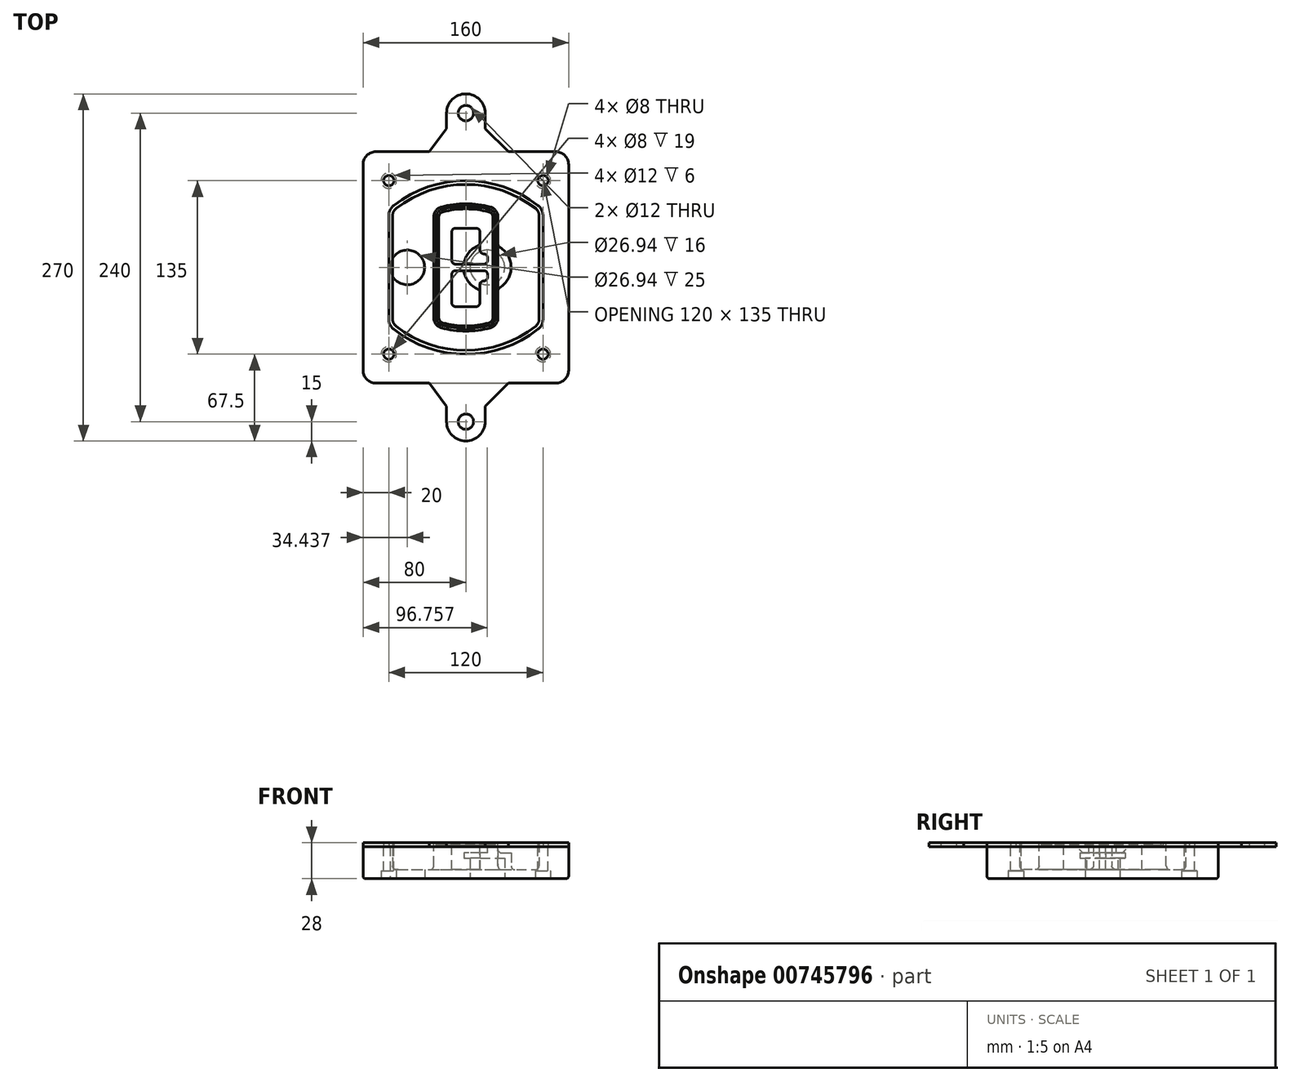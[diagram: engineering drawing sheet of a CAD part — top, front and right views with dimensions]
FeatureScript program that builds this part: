
annotation { "Feature Type Name" : "Feature", "Feature Type Description" : "" }
export const myFeature = defineFeature(function(context is Context, id is Id, definition is map)
    precondition{}
    {
        {
            var Q0;
            Q0=qCreatedBy(makeId("Top.planeOp"),FACE);
            var sketch = newSketch(context, id + "F0", { "sketchPlane" : qUnion([Q0])});
            skPoint(sketch, "E0.rect.middle", {"position": v(0, 0) * mm});
            skLineSegment(sketch, "E1.bottom", {"start": v(-70, -90) * mm, "end": v(70, -90) * mm});
            skLineSegment(sketch, "E1.top", {"start": v(-70, 90) * mm, "end": v(70, 90) * mm});
            skLineSegment(sketch, "E1.left", {"start": v(-80, -80) * mm, "end": v(-80, 80) * mm});
            skLineSegment(sketch, "E1.right", {"start": v(80, -80) * mm, "end": v(80, 80) * mm});
            skLineSegment(sketch, "E2", {"start": v(-80, 90) * mm, "end": v(80, -90) * mm, "construction": true});
            skLineSegment(sketch, "E3", {"start": v(80, 90) * mm, "end": v(-80, -90) * mm, "construction": true});
            skCircle(sketch, "E4", {"center": v(-60, 67.5) * mm, "radius": 4 * mm});
            skCircle(sketch, "E5", {"center": v(60, 67.5) * mm, "radius": 4 * mm});
            skCircle(sketch, "E6", {"center": v(60, -67.5) * mm, "radius": 4 * mm});
            skCircle(sketch, "E7", {"center": v(-60, -67.5) * mm, "radius": 4 * mm});
            skLineSegment(sketch, "E8", {"start": v(-60, 67.5) * mm, "end": v(60, 67.5) * mm, "construction": true});
            skLineSegment(sketch, "E9", {"start": v(60, 67.5) * mm, "end": v(60, -67.5) * mm, "construction": true});
            skLineSegment(sketch, "E10", {"start": v(60, -67.5) * mm, "end": v(-60, -67.5) * mm, "construction": true});
            skLineSegment(sketch, "E11", {"start": v(-60, -67.5) * mm, "end": v(-60, 67.5) * mm, "construction": true});
            skLineSegment(sketch, "E12", {"start": v(-60, 40.3) * mm, "end": v(-60, -40.3) * mm});
            skLineSegment(sketch, "E13", {"start": v(60, 40.3) * mm, "end": v(60, -40.3) * mm});
            skArc(sketch, "E14", {"start": v(56.15, 48.18) * mm, "mid": v(0, 67.5) * mm, "end": v(-56.15, 48.18) * mm});
            skArc(sketch, "E15", {"start": v(-56.15, -48.18) * mm, "mid": v(0, -67.5) * mm, "end": v(56.15, -48.18) * mm});
            skLineSegment(sketch, "E16", {"start": v(-60, 0) * mm, "end": v(60, 0) * mm, "construction": true});
            skPoint(sketch, "E17.visualSharp", {"position": v(-60, -45) * mm});
            skArc(sketch, "E17.filletArc", {"start": v(-60, -40.3) * mm, "mid": v(-58.99, -44.68) * mm, "end": v(-56.15, -48.18) * mm});
            skPoint(sketch, "E18.visualSharp", {"position": v(-60, 45) * mm});
            skArc(sketch, "E18.filletArc", {"start": v(-56.15, 48.18) * mm, "mid": v(-58.99, 44.68) * mm, "end": v(-60, 40.3) * mm});
            skPoint(sketch, "E19.visualSharp", {"position": v(60, 45) * mm});
            skArc(sketch, "E19.filletArc", {"start": v(60, 40.3) * mm, "mid": v(58.99, 44.68) * mm, "end": v(56.15, 48.18) * mm});
            skPoint(sketch, "E20.visualSharp", {"position": v(60, -45) * mm});
            skArc(sketch, "E20.filletArc", {"start": v(56.15, -48.18) * mm, "mid": v(58.99, -44.68) * mm, "end": v(60, -40.3) * mm});
            skPoint(sketch, "E21.visualSharp", {"position": v(-80, 90) * mm});
            skArc(sketch, "E21.filletArc", {"start": v(-70, 90) * mm, "mid": v(-77.07, 87.07) * mm, "end": v(-80, 80) * mm});
            skPoint(sketch, "E22.visualSharp", {"position": v(80, 90) * mm});
            skArc(sketch, "E22.filletArc", {"start": v(80, 80) * mm, "mid": v(77.07, 87.07) * mm, "end": v(70, 90) * mm});
            skPoint(sketch, "E23.visualSharp", {"position": v(80, -90) * mm});
            skArc(sketch, "E23.filletArc", {"start": v(70, -90) * mm, "mid": v(77.07, -87.07) * mm, "end": v(80, -80) * mm});
            skPoint(sketch, "E24.visualSharp", {"position": v(-80, -90) * mm});
            skArc(sketch, "E24.filletArc", {"start": v(-80, -80) * mm, "mid": v(-77.07, -87.07) * mm, "end": v(-70, -90) * mm});
            skArc(sketch, "E25.0", {"start": v(57, 40.3) * mm, "mid": v(56.3, 43.36) * mm, "end": v(54.3, 45.81) * mm});
            skLineSegment(sketch, "E25.1", {"start": v(57, 40.3) * mm, "end": v(57, -40.3) * mm});
            skArc(sketch, "E25.2", {"start": v(54.3, -45.81) * mm, "mid": v(56.3, -43.36) * mm, "end": v(57, -40.3) * mm});
            skArc(sketch, "E25.3", {"start": v(-54.3, -45.81) * mm, "mid": v(0, -64.5) * mm, "end": v(54.3, -45.81) * mm});
            skArc(sketch, "E25.4", {"start": v(-57, -40.3) * mm, "mid": v(-56.3, -43.36) * mm, "end": v(-54.3, -45.81) * mm});
            skArc(sketch, "E25.5", {"start": v(54.3, 45.81) * mm, "mid": v(0, 64.5) * mm, "end": v(-54.3, 45.81) * mm});
            skLineSegment(sketch, "E25.6", {"start": v(-57, 40.3) * mm, "end": v(-57, -40.3) * mm});
            skArc(sketch, "E25.7", {"start": v(-54.3, 45.81) * mm, "mid": v(-56.3, 43.36) * mm, "end": v(-57, 40.3) * mm});
            skArc(sketch, "E26.0", {"start": v(-58.62, 51.33) * mm, "mid": v(-62.58, 46.43) * mm, "end": v(-64, 40.3) * mm});
            skArc(sketch, "E26.1", {"start": v(58.62, 51.33) * mm, "mid": v(0, 71.5) * mm, "end": v(-58.62, 51.33) * mm});
            skArc(sketch, "E26.2", {"start": v(64, 40.3) * mm, "mid": v(62.58, 46.43) * mm, "end": v(58.62, 51.33) * mm});
            skLineSegment(sketch, "E26.3", {"start": v(64, 40.3) * mm, "end": v(64, -40.3) * mm});
            skArc(sketch, "E26.4", {"start": v(58.62, -51.33) * mm, "mid": v(62.58, -46.43) * mm, "end": v(64, -40.3) * mm});
            skLineSegment(sketch, "E26.5", {"start": v(-64, 40.3) * mm, "end": v(-64, -40.3) * mm});
            skArc(sketch, "E26.6", {"start": v(-58.62, -51.33) * mm, "mid": v(0, -71.5) * mm, "end": v(58.62, -51.33) * mm});
            skArc(sketch, "E26.7", {"start": v(-64, -40.3) * mm, "mid": v(-62.58, -46.43) * mm, "end": v(-58.62, -51.33) * mm});
            skSolve(sketch);
        }
        {
            var Q0;
            Q0=makeQuery(id+"F0.imprint","IMPRINT",FACE,{"disambiguationData":[TD([[makeQuery(id+"F0.imprint","IMPRINT",EDGE,{"derivedFrom":sQuery(id+"F0.wireOp",EDGE,"E1.bottom")}),1.0]])]});
            var Q1;
            Q1=makeQuery(id+"F0.imprint","IMPRINT",FACE,{"disambiguationData":[TD([[makeQuery(id+"F0.imprint","IMPRINT",EDGE,{"derivedFrom":sQuery(id+"F0.wireOp",EDGE,"E12")}),1.0]])]});
            var Q2;
            Q2=makeQuery(id+"F0.imprint","IMPRINT",FACE,{"disambiguationData":[TD([[makeQuery(id+"F0.imprint","IMPRINT",EDGE,{"derivedFrom":sQuery(id+"F0.wireOp",EDGE,"E25.0")}),1.0]])]});
            var Q3;
            Q3=makeQuery(id+"F0.imprint","IMPRINT",FACE,{"disambiguationData":[TD([[makeQuery(id+"F0.imprint","IMPRINT",EDGE,{"derivedFrom":sQuery(id+"F0.wireOp",EDGE,"E12")}),-1.0]])]});
            extrude(context, id + "F1", {"entities" : qUnion([Q0, Q1, Q2, Q3]), "oppositeDirection" : true, "depth" : 25 * mm});
        }
        {
            var Q0;
            Q0=makeQuery(id+"F0.imprint","IMPRINT",FACE,{"disambiguationData":[TD([[makeQuery(id+"F0.imprint","IMPRINT",EDGE,{"derivedFrom":sQuery(id+"F0.wireOp",EDGE,"E12")}),1.0]])]});
            extrude(context, id + "F2", {"entities" : qUnion([Q0]), "operationType" : NewBodyOperationType.ADD, "depth" : 3 * mm, "offsetDistance" : 25 * mm});
        }
        {
            var Q0;
            Q0=makeQuery(id+"F0.imprint","IMPRINT",FACE,{"disambiguationData":[TD([[makeQuery(id+"F0.imprint","IMPRINT",EDGE,{"derivedFrom":sQuery(id+"F0.wireOp",EDGE,"E25.0")}),1.0]])]});
            extrude(context, id + "F3", {"entities" : qUnion([Q0]), "operationType" : NewBodyOperationType.REMOVE, "oppositeDirection" : true, "depth" : 18 * mm});
        }
        {
            var Q0;
            Q0=makeQuery(id+"F2.opExtrude","CAP_FACE",FACE,{"disambiguationData":[OSD([sQuery(id+"F0.wireOp",EDGE,"E12"),sQuery(id+"F0.wireOp",EDGE,"E13"),sQuery(id+"F0.wireOp",EDGE,"E14"),sQuery(id+"F0.wireOp",EDGE,"E15"),sQuery(id+"F0.wireOp",EDGE,"E17.filletArc"),sQuery(id+"F0.wireOp",EDGE,"E18.filletArc"),sQuery(id+"F0.wireOp",EDGE,"E19.filletArc"),sQuery(id+"F0.wireOp",EDGE,"E20.filletArc"),sQuery(id+"F0.wireOp",EDGE,"E25.0"),sQuery(id+"F0.wireOp",EDGE,"E25.1"),sQuery(id+"F0.wireOp",EDGE,"E25.2"),sQuery(id+"F0.wireOp",EDGE,"E25.3"),sQuery(id+"F0.wireOp",EDGE,"E25.4"),sQuery(id+"F0.wireOp",EDGE,"E25.5"),sQuery(id+"F0.wireOp",EDGE,"E25.6"),sQuery(id+"F0.wireOp",EDGE,"E25.7")])],"isStart":false});
            var sketch = newSketch(context, id + "F4", { "sketchPlane" : qUnion([Q0])});
            skArc(sketch, "E27.0", {"start": v(-19.08, -46.97) * mm, "mid": v(0, -49.5) * mm, "end": v(19.08, -46.97) * mm});
            skArc(sketch, "E28.0", {"start": v(19.08, 46.97) * mm, "mid": v(0, 49.5) * mm, "end": v(-19.08, 46.97) * mm});
            skLineSegment(sketch, "E29", {"start": v(-25, 39.25) * mm, "end": v(-25, -39.25) * mm});
            skLineSegment(sketch, "E30", {"start": v(25, 39.25) * mm, "end": v(25, -39.25) * mm});
            skLineSegment(sketch, "E31", {"start": v(-25, 45.1) * mm, "end": v(25, 45.1) * mm, "construction": true});
            skLineSegment(sketch, "E32", {"start": v(-25, -45.1) * mm, "end": v(25, -45.1) * mm, "construction": true});
            skPoint(sketch, "E33.visualSharp", {"position": v(-25, 45.1) * mm});
            skArc(sketch, "E33.filletArc", {"start": v(-19.08, 46.97) * mm, "mid": v(-23.35, 44.11) * mm, "end": v(-25, 39.25) * mm});
            skPoint(sketch, "E34.visualSharp", {"position": v(25, 45.1) * mm});
            skArc(sketch, "E34.filletArc", {"start": v(25, 39.25) * mm, "mid": v(23.35, 44.11) * mm, "end": v(19.08, 46.97) * mm});
            skPoint(sketch, "E35.visualSharp", {"position": v(25, -45.1) * mm});
            skArc(sketch, "E35.filletArc", {"start": v(19.08, -46.97) * mm, "mid": v(23.35, -44.11) * mm, "end": v(25, -39.25) * mm});
            skPoint(sketch, "E36.visualSharp", {"position": v(-25, -45.1) * mm});
            skArc(sketch, "E36.filletArc", {"start": v(-25, -39.25) * mm, "mid": v(-23.35, -44.11) * mm, "end": v(-19.08, -46.97) * mm});
            skArc(sketch, "E37.0", {"start": v(54.3, 45.81) * mm, "mid": v(0, 64.5) * mm, "end": v(-54.3, 45.81) * mm});
            skArc(sketch, "E37.1", {"start": v(-54.3, 45.81) * mm, "mid": v(-56.3, 43.36) * mm, "end": v(-57, 40.3) * mm});
            skLineSegment(sketch, "E37.2", {"start": v(-57, 40.3) * mm, "end": v(-57, -40.3) * mm});
            skArc(sketch, "E37.3", {"start": v(-57, -40.3) * mm, "mid": v(-56.3, -43.36) * mm, "end": v(-54.3, -45.81) * mm});
            skArc(sketch, "E37.4", {"start": v(-54.3, -45.81) * mm, "mid": v(0, -64.5) * mm, "end": v(54.3, -45.81) * mm});
            skArc(sketch, "E37.5", {"start": v(54.3, -45.81) * mm, "mid": v(56.3, -43.36) * mm, "end": v(57, -40.3) * mm});
            skLineSegment(sketch, "E37.6", {"start": v(57, 40.3) * mm, "end": v(57, -40.3) * mm});
            skArc(sketch, "E37.7", {"start": v(57, 40.3) * mm, "mid": v(56.3, 43.36) * mm, "end": v(54.3, 45.81) * mm});
            skLineSegment(sketch, "E38.0", {"start": v(23, 39.25) * mm, "end": v(23, -39.25) * mm});
            skArc(sketch, "E38.1", {"start": v(18.56, -45.04) * mm, "mid": v(21.76, -42.9) * mm, "end": v(23, -39.25) * mm});
            skArc(sketch, "E38.2", {"start": v(-18.56, -45.04) * mm, "mid": v(0, -47.5) * mm, "end": v(18.56, -45.04) * mm});
            skArc(sketch, "E38.3", {"start": v(-23, -39.25) * mm, "mid": v(-21.76, -42.9) * mm, "end": v(-18.56, -45.04) * mm});
            skLineSegment(sketch, "E38.4", {"start": v(-23, 39.25) * mm, "end": v(-23, -39.25) * mm});
            skArc(sketch, "E38.5", {"start": v(23, 39.25) * mm, "mid": v(21.76, 42.9) * mm, "end": v(18.56, 45.04) * mm});
            skArc(sketch, "E38.6", {"start": v(-18.56, 45.04) * mm, "mid": v(-21.76, 42.9) * mm, "end": v(-23, 39.25) * mm});
            skArc(sketch, "E38.7", {"start": v(18.56, 45.04) * mm, "mid": v(0, 47.5) * mm, "end": v(-18.56, 45.04) * mm});
            skArc(sketch, "E39.0", {"start": v(21, 39.25) * mm, "mid": v(20.18, 41.68) * mm, "end": v(18.04, 43.1) * mm});
            skLineSegment(sketch, "E39.1", {"start": v(21, 39.25) * mm, "end": v(21, -39.25) * mm});
            skArc(sketch, "E39.2", {"start": v(18.04, -43.1) * mm, "mid": v(20.18, -41.68) * mm, "end": v(21, -39.25) * mm});
            skArc(sketch, "E39.3", {"start": v(-18.04, -43.1) * mm, "mid": v(0, -45.5) * mm, "end": v(18.04, -43.1) * mm});
            skArc(sketch, "E39.4", {"start": v(-21, -39.25) * mm, "mid": v(-20.18, -41.68) * mm, "end": v(-18.04, -43.1) * mm});
            skArc(sketch, "E39.5", {"start": v(18.04, 43.1) * mm, "mid": v(0, 45.5) * mm, "end": v(-18.04, 43.1) * mm});
            skLineSegment(sketch, "E39.6", {"start": v(-21, 39.25) * mm, "end": v(-21, -39.25) * mm});
            skArc(sketch, "E39.7", {"start": v(-18.04, 43.1) * mm, "mid": v(-20.18, 41.68) * mm, "end": v(-21, 39.25) * mm});
            skLineSegment(sketch, "E40", {"start": v(-25, 0) * mm, "end": v(25, 0) * mm, "construction": true});
            skLineSegment(sketch, "E41", {"start": v(-11, 5.5) * mm, "end": v(-11, 27.5) * mm});
            skLineSegment(sketch, "E42", {"start": v(-8, 30.5) * mm, "end": v(8, 30.5) * mm});
            skLineSegment(sketch, "E43", {"start": v(11, 27.5) * mm, "end": v(11, 13.5) * mm});
            skLineSegment(sketch, "E44", {"start": v(14, 10.5) * mm, "end": v(14, 10.5) * mm});
            skLineSegment(sketch, "E45", {"start": v(17, 7.5) * mm, "end": v(17, 5.5) * mm});
            skLineSegment(sketch, "E46", {"start": v(14, 2.5) * mm, "end": v(-8, 2.5) * mm});
            skPoint(sketch, "E47.visualSharp", {"position": v(-11, 30.5) * mm});
            skArc(sketch, "E47.filletArc", {"start": v(-8, 30.5) * mm, "mid": v(-10.12, 29.62) * mm, "end": v(-11, 27.5) * mm});
            skPoint(sketch, "E48.visualSharp", {"position": v(11, 30.5) * mm});
            skArc(sketch, "E48.filletArc", {"start": v(11, 27.5) * mm, "mid": v(10.12, 29.62) * mm, "end": v(8, 30.5) * mm});
            skPoint(sketch, "E49.visualSharp", {"position": v(11, 10.5) * mm});
            skArc(sketch, "E49.filletArc", {"start": v(11, 13.5) * mm, "mid": v(11.88, 11.38) * mm, "end": v(14, 10.5) * mm});
            skPoint(sketch, "E50.visualSharp", {"position": v(17, 10.5) * mm});
            skArc(sketch, "E50.filletArc", {"start": v(17, 7.5) * mm, "mid": v(16.12, 9.62) * mm, "end": v(14, 10.5) * mm});
            skPoint(sketch, "E51.visualSharp", {"position": v(17, 2.5) * mm});
            skArc(sketch, "E51.filletArc", {"start": v(14, 2.5) * mm, "mid": v(16.12, 3.38) * mm, "end": v(17, 5.5) * mm});
            skPoint(sketch, "E52.visualSharp", {"position": v(-11, 2.5) * mm});
            skArc(sketch, "E52.filletArc", {"start": v(-11, 5.5) * mm, "mid": v(-10.12, 3.38) * mm, "end": v(-8, 2.5) * mm});
            skLineSegment(sketch, "E53.0.MirrorCS", {"start": v(14, -2.5) * mm, "end": v(-8, -2.5) * mm});
            skArc(sketch, "E54.0.MirrorCS", {"start": v(-11, -5.5) * mm, "mid": v(-10.12, -3.38) * mm, "end": v(-8, -2.5) * mm});
            skLineSegment(sketch, "E55.0.MirrorCS", {"start": v(-11, -5.5) * mm, "end": v(-11, -27.5) * mm});
            skArc(sketch, "E56.0.MirrorCS", {"start": v(-8, -30.5) * mm, "mid": v(-10.12, -29.62) * mm, "end": v(-11, -27.5) * mm});
            skLineSegment(sketch, "E57.0.MirrorCS", {"start": v(-8, -30.5) * mm, "end": v(8, -30.5) * mm});
            skArc(sketch, "E58.0.MirrorCS", {"start": v(11, -27.5) * mm, "mid": v(10.12, -29.62) * mm, "end": v(8, -30.5) * mm});
            skLineSegment(sketch, "E59.0.MirrorCS", {"start": v(11, -27.5) * mm, "end": v(11, -13.5) * mm});
            skArc(sketch, "E60.0.MirrorCS", {"start": v(11, -13.5) * mm, "mid": v(11.88, -11.38) * mm, "end": v(14, -10.5) * mm});
            skArc(sketch, "E61.0.MirrorCS", {"start": v(17, -7.5) * mm, "mid": v(16.12, -9.62) * mm, "end": v(14, -10.5) * mm});
            skLineSegment(sketch, "E62.0.MirrorCS", {"start": v(17, -7.5) * mm, "end": v(17, -5.5) * mm});
            skArc(sketch, "E63.0.MirrorCS", {"start": v(14, -2.5) * mm, "mid": v(16.12, -3.38) * mm, "end": v(17, -5.5) * mm});
            skSolve(sketch);
        }
        {
            var Q0;
            Q0=makeQuery(id+"F4.imprint","IMPRINT",FACE,{"disambiguationData":[TD([[makeQuery(id+"F4.imprint","IMPRINT",EDGE,{"derivedFrom":sQuery(id+"F4.wireOp",EDGE,"E27.0")}),1.0]])]});
            var Q1;
            Q1=makeQuery(id+"F4.imprint","IMPRINT",FACE,{"disambiguationData":[TD([[makeQuery(id+"F4.imprint","IMPRINT",EDGE,{"derivedFrom":sQuery(id+"F4.wireOp",EDGE,"E38.0")}),-1.0]])]});
            var Q2;
            Q2=makeQuery(id+"F4.imprint","IMPRINT",FACE,{"disambiguationData":[TD([[makeQuery(id+"F4.imprint","IMPRINT",EDGE,{"derivedFrom":sQuery(id+"F4.wireOp",EDGE,"E39.0")}),1.0]])]});
            extrude(context, id + "F5", {"entities" : qUnion([Q0, Q1, Q2]), "operationType" : NewBodyOperationType.ADD, "endBound" : BoundingType.UP_TO_NEXT, "oppositeDirection" : true, "depth" : 25 * mm});
        }
        {
            var Q0;
            Q0=makeQuery(id+"F4.imprint","IMPRINT",FACE,{"disambiguationData":[TD([[makeQuery(id+"F4.imprint","IMPRINT",EDGE,{"derivedFrom":sQuery(id+"F4.wireOp",EDGE,"E38.0")}),-1.0]])]});
            extrude(context, id + "F6", {"entities" : qUnion([Q0]), "operationType" : NewBodyOperationType.REMOVE, "oppositeDirection" : true, "depth" : 2 * mm});
        }
        {
            var Q0;
            Q0=makeQuery(id+"F1.opExtrude","CAP_FACE",FACE,{"disambiguationData":[OSD([sQuery(id+"F0.wireOp",EDGE,"E1.bottom"),sQuery(id+"F0.wireOp",EDGE,"E1.top"),sQuery(id+"F0.wireOp",EDGE,"E1.left"),sQuery(id+"F0.wireOp",EDGE,"E1.right"),sQuery(id+"F0.wireOp",EDGE,"E4"),sQuery(id+"F0.wireOp",EDGE,"E5"),sQuery(id+"F0.wireOp",EDGE,"E6"),sQuery(id+"F0.wireOp",EDGE,"E7"),sQuery(id+"F0.wireOp",EDGE,"E21.filletArc"),sQuery(id+"F0.wireOp",EDGE,"E22.filletArc"),sQuery(id+"F0.wireOp",EDGE,"E23.filletArc"),sQuery(id+"F0.wireOp",EDGE,"E24.filletArc")])],"isStart":false});
            var sketch = newSketch(context, id + "F7", { "sketchPlane" : qUnion([Q0])});
            skCircle(sketch, "E64", {"center": v(16.76, 0) * mm, "radius": 13.47 * mm});
            skCircle(sketch, "E65", {"center": v(-45.56, 0) * mm, "radius": 13.47 * mm});
            skLineSegment(sketch, "E66", {"start": v(80, 0) * mm, "end": v(-80, 0) * mm});
            skCircle(sketch, "E67", {"center": v(16.76, 0) * mm, "radius": 18.47 * mm});
            skCircle(sketch, "E68", {"center": v(60, -67.5) * mm, "radius": 6 * mm});
            skCircle(sketch, "E69", {"center": v(-60, -67.5) * mm, "radius": 6 * mm});
            skCircle(sketch, "E70", {"center": v(-60, 67.5) * mm, "radius": 6 * mm});
            skCircle(sketch, "E71", {"center": v(60, 67.5) * mm, "radius": 6 * mm});
            skSolve(sketch);
        }
        {
            var Q0;
            {var subQ1=sQuery(id+"F7.wireOp",EDGE,"E66");var subQ4=sQuery(id+"F7.wireOp",EDGE,"E64");var subQ6=makeQuery(id+"F7.imprint","INTERSECT",VERTEX,{"disambiguationData":[OD(0.0)],"derivedFrom":[subQ4,subQ1]});Q0=makeQuery(id+"F7.imprint","IMPRINT",FACE,{"disambiguationData":[TD([[makeQuery(id+"F7.imprint","IMPRINT",EDGE,{"disambiguationData":[TD([[subQ6,-1.0]])],"derivedFrom":subQ4}),-1.0]])]});}
            var Q1;
            {var subQ0=sQuery(id+"F7.wireOp",EDGE,"E66");var subQ1=sQuery(id+"F7.wireOp",EDGE,"E64");var subQ3=makeQuery(id+"F7.imprint","INTERSECT",VERTEX,{"disambiguationData":[OD(0.0)],"derivedFrom":[subQ1,subQ0]});Q1=makeQuery(id+"F7.imprint","IMPRINT",FACE,{"disambiguationData":[TD([[makeQuery(id+"F7.imprint","IMPRINT",EDGE,{"disambiguationData":[TD([[subQ3,-1.0]])],"derivedFrom":subQ1}),1.0]])]});}
            var Q2;
            {var subQ0=sQuery(id+"F7.wireOp",EDGE,"E66");var subQ1=sQuery(id+"F7.wireOp",EDGE,"E64");var subQ3=makeQuery(id+"F7.imprint","INTERSECT",VERTEX,{"disambiguationData":[OD(0.0)],"derivedFrom":[subQ1,subQ0]});Q2=makeQuery(id+"F7.imprint","IMPRINT",FACE,{"disambiguationData":[TD([[makeQuery(id+"F7.imprint","IMPRINT",EDGE,{"disambiguationData":[TD([[subQ3,1.0]])],"derivedFrom":subQ1}),1.0]])]});}
            var Q3;
            {var subQ1=sQuery(id+"F7.wireOp",EDGE,"E66");var subQ4=sQuery(id+"F7.wireOp",EDGE,"E64");var subQ6=makeQuery(id+"F7.imprint","INTERSECT",VERTEX,{"disambiguationData":[OD(0.0)],"derivedFrom":[subQ4,subQ1]});Q3=makeQuery(id+"F7.imprint","IMPRINT",FACE,{"disambiguationData":[TD([[makeQuery(id+"F7.imprint","IMPRINT",EDGE,{"disambiguationData":[TD([[subQ6,1.0]])],"derivedFrom":subQ4}),-1.0]])]});}
            extrude(context, id + "F8", {"entities" : qUnion([Q0, Q1, Q2, Q3]), "operationType" : NewBodyOperationType.ADD, "oppositeDirection" : true, "depth" : 20 * mm});
        }
        {
            var Q0;
            {var subQ0=sQuery(id+"F7.wireOp",EDGE,"E66");var subQ1=sQuery(id+"F7.wireOp",EDGE,"E64");var subQ3=makeQuery(id+"F7.imprint","INTERSECT",VERTEX,{"disambiguationData":[OD(0.0)],"derivedFrom":[subQ1,subQ0]});Q0=makeQuery(id+"F7.imprint","IMPRINT",FACE,{"disambiguationData":[TD([[makeQuery(id+"F7.imprint","IMPRINT",EDGE,{"disambiguationData":[TD([[subQ3,-1.0]])],"derivedFrom":subQ1}),1.0]])]});}
            var Q1;
            {var subQ0=sQuery(id+"F7.wireOp",EDGE,"E66");var subQ1=sQuery(id+"F7.wireOp",EDGE,"E64");var subQ3=makeQuery(id+"F7.imprint","INTERSECT",VERTEX,{"disambiguationData":[OD(0.0)],"derivedFrom":[subQ1,subQ0]});Q1=makeQuery(id+"F7.imprint","IMPRINT",FACE,{"disambiguationData":[TD([[makeQuery(id+"F7.imprint","IMPRINT",EDGE,{"disambiguationData":[TD([[subQ3,1.0]])],"derivedFrom":subQ1}),1.0]])]});}
            extrude(context, id + "F9", {"entities" : qUnion([Q0, Q1]), "operationType" : NewBodyOperationType.REMOVE, "oppositeDirection" : true, "depth" : 16 * mm});
        }
        {
            var Q0;
            {var subQ0=sQuery(id+"F7.wireOp",EDGE,"E66");var subQ1=sQuery(id+"F7.wireOp",EDGE,"E65");var subQ3=makeQuery(id+"F7.imprint","INTERSECT",VERTEX,{"disambiguationData":[OD(0.0)],"derivedFrom":[subQ1,subQ0]});Q0=makeQuery(id+"F7.imprint","IMPRINT",FACE,{"disambiguationData":[TD([[makeQuery(id+"F7.imprint","IMPRINT",EDGE,{"disambiguationData":[TD([[subQ3,-1.0]])],"derivedFrom":subQ1}),1.0]])]});}
            var Q1;
            {var subQ0=sQuery(id+"F7.wireOp",EDGE,"E66");var subQ1=sQuery(id+"F7.wireOp",EDGE,"E65");var subQ3=makeQuery(id+"F7.imprint","INTERSECT",VERTEX,{"disambiguationData":[OD(0.0)],"derivedFrom":[subQ1,subQ0]});Q1=makeQuery(id+"F7.imprint","IMPRINT",FACE,{"disambiguationData":[TD([[makeQuery(id+"F7.imprint","IMPRINT",EDGE,{"disambiguationData":[TD([[subQ3,1.0]])],"derivedFrom":subQ1}),1.0]])]});}
            extrude(context, id + "F10", {"entities" : qUnion([Q0, Q1]), "operationType" : NewBodyOperationType.REMOVE, "oppositeDirection" : true, "depth" : 25 * mm});
        }
        {
            var Q0;
            Q0=makeQuery(id+"F7.imprint","IMPRINT",FACE,{"disambiguationData":[TD([[makeQuery(id+"F7.imprint","IMPRINT",EDGE,{"derivedFrom":sQuery(id+"F7.wireOp",EDGE,"E68")}),1.0]])]});
            var Q1;
            Q1=makeQuery(id+"F7.imprint","IMPRINT",FACE,{"disambiguationData":[TD([[makeQuery(id+"F7.imprint","IMPRINT",EDGE,{"derivedFrom":makeQuery(id+"F1.opExtrude","CAP_EDGE",EDGE,{"disambiguationData":[OSD([sQuery(id+"F0.wireOp",EDGE,"E5")])],"isStart":false})}),-1.0]])]});
            var Q2;
            Q2=makeQuery(id+"F7.imprint","IMPRINT",FACE,{"disambiguationData":[TD([[makeQuery(id+"F7.imprint","IMPRINT",EDGE,{"derivedFrom":sQuery(id+"F7.wireOp",EDGE,"E69")}),1.0]])]});
            var Q3;
            Q3=makeQuery(id+"F7.imprint","IMPRINT",FACE,{"disambiguationData":[TD([[makeQuery(id+"F7.imprint","IMPRINT",EDGE,{"derivedFrom":makeQuery(id+"F1.opExtrude","CAP_EDGE",EDGE,{"disambiguationData":[OSD([sQuery(id+"F0.wireOp",EDGE,"E4")])],"isStart":false})}),-1.0]])]});
            var Q4;
            Q4=makeQuery(id+"F7.imprint","IMPRINT",FACE,{"disambiguationData":[TD([[makeQuery(id+"F7.imprint","IMPRINT",EDGE,{"derivedFrom":sQuery(id+"F7.wireOp",EDGE,"E70")}),1.0]])]});
            var Q5;
            Q5=makeQuery(id+"F7.imprint","IMPRINT",FACE,{"disambiguationData":[TD([[makeQuery(id+"F7.imprint","IMPRINT",EDGE,{"derivedFrom":makeQuery(id+"F1.opExtrude","CAP_EDGE",EDGE,{"disambiguationData":[OSD([sQuery(id+"F0.wireOp",EDGE,"E7")])],"isStart":false})}),-1.0]])]});
            var Q6;
            Q6=makeQuery(id+"F7.imprint","IMPRINT",FACE,{"disambiguationData":[TD([[makeQuery(id+"F7.imprint","IMPRINT",EDGE,{"derivedFrom":sQuery(id+"F7.wireOp",EDGE,"E71")}),1.0]])]});
            var Q7;
            Q7=makeQuery(id+"F7.imprint","IMPRINT",FACE,{"disambiguationData":[TD([[makeQuery(id+"F7.imprint","IMPRINT",EDGE,{"derivedFrom":makeQuery(id+"F1.opExtrude","CAP_EDGE",EDGE,{"disambiguationData":[OSD([sQuery(id+"F0.wireOp",EDGE,"E6")])],"isStart":false})}),-1.0]])]});
            extrude(context, id + "F11", {"entities" : qUnion([Q0, Q1, Q2, Q3, Q4, Q5, Q6, Q7]), "operationType" : NewBodyOperationType.REMOVE, "oppositeDirection" : true, "depth" : 6 * mm});
        }
        {
            var Q0;
            Q0=makeQuery(id+"F9.boolean.opBoolean","COPY",FACE,{"derivedFrom":makeQuery(id+"F9.opExtrude","CAP_FACE",FACE,{"disambiguationData":[OSD([sQuery(id+"F7.wireOp",EDGE,"E64")])],"isStart":false})});
            var sketch = newSketch(context, id + "F12", { "sketchPlane" : qUnion([Q0])});
            skArc(sketch, "E72.0", {"start": v(11, 17.55) * mm, "mid": v(2.57, 11.82) * mm, "end": v(-1.54, 2.5) * mm});
            skArc(sketch, "E72.1", {"start": v(-1.54, -2.5) * mm, "mid": v(2.57, -11.82) * mm, "end": v(11, -17.55) * mm});
            skLineSegment(sketch, "E73", {"start": v(-1.54, -2.5) * mm, "end": v(14, -2.5) * mm});
            skLineSegment(sketch, "E74.0", {"start": v(14, 2.5) * mm, "end": v(-1.54, 2.5) * mm});
            skArc(sketch, "E74.1", {"start": v(14, 2.5) * mm, "mid": v(16.12, 3.38) * mm, "end": v(17, 5.5) * mm});
            skLineSegment(sketch, "E74.2", {"start": v(17, 7.5) * mm, "end": v(17, 5.5) * mm});
            skArc(sketch, "E74.3", {"start": v(17, 7.5) * mm, "mid": v(16.12, 9.62) * mm, "end": v(14, 10.5) * mm});
            skArc(sketch, "E74.4", {"start": v(11, 13.5) * mm, "mid": v(11.88, 11.38) * mm, "end": v(14, 10.5) * mm});
            skLineSegment(sketch, "E74.5", {"start": v(11, 17.55) * mm, "end": v(11, 13.5) * mm});
            skLineSegment(sketch, "E74.7", {"start": v(14, -2.5) * mm, "end": v(-1.54, -2.5) * mm});
            skArc(sketch, "E74.8", {"start": v(14, -2.5) * mm, "mid": v(16.12, -3.38) * mm, "end": v(17, -5.5) * mm});
            skLineSegment(sketch, "E74.9", {"start": v(17, -7.5) * mm, "end": v(17, -5.5) * mm});
            skArc(sketch, "E74.10", {"start": v(17, -7.5) * mm, "mid": v(16.12, -9.62) * mm, "end": v(14, -10.5) * mm});
            skArc(sketch, "E74.11", {"start": v(11, -13.5) * mm, "mid": v(11.88, -11.38) * mm, "end": v(14, -10.5) * mm});
            skLineSegment(sketch, "E74.12", {"start": v(11, -17.55) * mm, "end": v(11, -13.5) * mm});
            skPoint(sketch, "E75.orphan", {"position": v(11, -27.5) * mm});
            skPoint(sketch, "E76.orphan", {"position": v(-8, -2.5) * mm});
            skPoint(sketch, "E77.orphan", {"position": v(-8, 2.5) * mm});
            skPoint(sketch, "E78.orphan", {"position": v(11, 27.5) * mm});
            skSolve(sketch);
        }
        {
            var Q0;
            {var subQ7=sQuery(id+"F12.wireOp",EDGE,"E72.0");var subQ14=sQuery(id+"F12.wireOp",EDGE,"E72.1");var subQ16=sQuery(id+"F12.wireOp",EDGE,"E74.1");var subQ18=sQuery(id+"F12.wireOp",EDGE,"E74.8");Q0=qUnion([makeQuery(id+"F12.imprint","IMPRINT",FACE,{"disambiguationData":[TD([[makeQuery(id+"F12.imprint","IMPRINT",EDGE,{"derivedFrom":subQ7}),1.0]])]}),makeQuery(id+"F12.imprint","IMPRINT",FACE,{"disambiguationData":[TD([[makeQuery(id+"F12.imprint","IMPRINT",EDGE,{"derivedFrom":subQ14}),1.0]])]}),makeQuery(id+"F12.imprint","IMPRINT",FACE,{"disambiguationData":[TD([[makeQuery(id+"F12.imprint","IMPRINT",EDGE,{"derivedFrom":subQ16}),1.0]])]}),makeQuery(id+"F12.imprint","IMPRINT",FACE,{"disambiguationData":[TD([[makeQuery(id+"F12.imprint","IMPRINT",EDGE,{"derivedFrom":subQ18}),-1.0]])]})]);}
            var Q1;
            Q1=makeQuery(id+"F5.boolean.opBoolean","SPLIT",FACE,{"disambiguationData":[TD([makeQuery(id+"F5.opExtrude","SWEPT_FACE",FACE,{"disambiguationData":[OSD([sQuery(id+"F4.wireOp",EDGE,"E41")])]})])],"derivedFrom":makeQuery(id+"F3.boolean.opBoolean","COPY",FACE,{"derivedFrom":makeQuery(id+"F3.opExtrude","CAP_FACE",FACE,{"disambiguationData":[OSD([sQuery(id+"F0.wireOp",EDGE,"E25.0"),sQuery(id+"F0.wireOp",EDGE,"E25.1"),sQuery(id+"F0.wireOp",EDGE,"E25.2"),sQuery(id+"F0.wireOp",EDGE,"E25.3"),sQuery(id+"F0.wireOp",EDGE,"E25.4"),sQuery(id+"F0.wireOp",EDGE,"E25.5"),sQuery(id+"F0.wireOp",EDGE,"E25.6"),sQuery(id+"F0.wireOp",EDGE,"E25.7")])],"isStart":false})})});
            extrude(context, id + "F13", {"entities" : qUnion([Q0]), "operationType" : NewBodyOperationType.REMOVE, "endBound" : BoundingType.UP_TO_SURFACE, "endBoundEntityFace" : qUnion([Q1]), "depth" : 25 * mm});
        }
        {
            var Q0;
            Q0=makeQuery(id+"F3.boolean.opBoolean","COPY",EDGE,{"derivedFrom":makeQuery(id+"F3.opExtrude","CAP_EDGE",EDGE,{"disambiguationData":[OSD([sQuery(id+"F0.wireOp",EDGE,"E25.6")])],"isStart":false})});
            var Q1;
            Q1=makeQuery(id+"F8.boolean.opBoolean","INTERSECT",EDGE,{"derivedFrom":[makeQuery(id+"F5.opExtrude","SWEPT_FACE",FACE,{"disambiguationData":[OSD([sQuery(id+"F4.wireOp",EDGE,"E30")])]}),makeQuery(id+"F8.opExtrude","CAP_FACE",FACE,{"disambiguationData":[OSD([sQuery(id+"F7.wireOp",EDGE,"E67")])],"isStart":false})]});
            var Q2;
            Q2=makeQuery(id+"F8.boolean.opBoolean","INTERSECT",EDGE,{"disambiguationData":[OD(1.0)],"derivedFrom":[makeQuery(id+"F5.opExtrude","SWEPT_FACE",FACE,{"disambiguationData":[OSD([sQuery(id+"F4.wireOp",EDGE,"E30")])]}),makeQuery(id+"F8.opExtrude","SWEPT_FACE",FACE,{"disambiguationData":[OSD([sQuery(id+"F7.wireOp",EDGE,"E67")])]})]});
            var Q3;
            {var subQ0=sQuery(id+"F4.wireOp",EDGE,"E30");Q3=makeQuery(id+"F8.boolean.opBoolean","SPLIT",EDGE,{"disambiguationData":[TD([makeQuery(id+"F5.opExtrude","SWEPT_FACE",FACE,{"disambiguationData":[OSD([sQuery(id+"F4.wireOp",EDGE,"E35.filletArc")])]})])],"derivedFrom":makeQuery(id+"F5.opExtrude","CAP_EDGE",EDGE,{"disambiguationData":[OSD([subQ0])],"isStart":false})});}
            var Q4;
            {var subQ0=sQuery(id+"F0.wireOp",EDGE,"E25.7");var subQ1=sQuery(id+"F0.wireOp",EDGE,"E25.1");var subQ2=sQuery(id+"F0.wireOp",EDGE,"E25.6");var subQ3=sQuery(id+"F0.wireOp",EDGE,"E25.5");var subQ4=sQuery(id+"F0.wireOp",EDGE,"E25.4");var subQ5=sQuery(id+"F0.wireOp",EDGE,"E25.0");var subQ6=sQuery(id+"F0.wireOp",EDGE,"E25.2");var subQ7=sQuery(id+"F0.wireOp",EDGE,"E25.3");Q4=makeQuery(id+"F8.boolean.opBoolean","INTERSECT",EDGE,{"derivedFrom":[makeQuery(id+"F5.boolean.opBoolean","SPLIT",FACE,{"disambiguationData":[TD([makeQuery(id+"F2.opExtrude","SWEPT_FACE",FACE,{"disambiguationData":[OSD([subQ5])]})])],"derivedFrom":makeQuery(id+"F3.boolean.opBoolean","COPY",FACE,{"derivedFrom":makeQuery(id+"F3.opExtrude","CAP_FACE",FACE,{"disambiguationData":[OSD([subQ5,subQ1,subQ6,subQ7,subQ4,subQ3,subQ2,subQ0])],"isStart":false})})}),makeQuery(id+"F8.opExtrude","SWEPT_FACE",FACE,{"disambiguationData":[OSD([sQuery(id+"F7.wireOp",EDGE,"E67")])]})]});}
            var Q5;
            Q5=makeQuery(id+"F8.boolean.opBoolean","INTERSECT",EDGE,{"disambiguationData":[OD(0.0)],"derivedFrom":[makeQuery(id+"F5.opExtrude","SWEPT_FACE",FACE,{"disambiguationData":[OSD([sQuery(id+"F4.wireOp",EDGE,"E30")])]}),makeQuery(id+"F8.opExtrude","SWEPT_FACE",FACE,{"disambiguationData":[OSD([sQuery(id+"F7.wireOp",EDGE,"E67")])]})]});
            fillet(context, id + "F14", {"entities" : qUnion([Q0, Q1, Q2, Q3, Q4, Q5]), "radius" : 3 * mm, "tangentPropagation" : true, "allowEdgeOverflow" : false});
        }
        {
            var Q0;
            Q0=makeQuery(id+"F1.opExtrude","CAP_EDGE",EDGE,{"disambiguationData":[OSD([sQuery(id+"F0.wireOp",EDGE,"E1.bottom")])],"isStart":false});
            fillet(context, id + "F15", {"entities" : qUnion([Q0]), "radius" : 2 * mm, "tangentPropagation" : true, "allowEdgeOverflow" : false});
        }
        {
            var Q0;
            {var subQ0=sQuery(id+"F0.wireOp",EDGE,"E21.filletArc");var subQ1=sQuery(id+"F0.wireOp",EDGE,"E7");var subQ2=sQuery(id+"F0.wireOp",EDGE,"E6");var subQ3=sQuery(id+"F0.wireOp",EDGE,"E5");var subQ4=sQuery(id+"F0.wireOp",EDGE,"E4");var subQ5=sQuery(id+"F0.wireOp",EDGE,"E22.filletArc");var subQ6=sQuery(id+"F0.wireOp",EDGE,"E1.bottom");var subQ7=sQuery(id+"F0.wireOp",EDGE,"E1.right");var subQ8=sQuery(id+"F0.wireOp",EDGE,"E1.top");var subQ9=sQuery(id+"F0.wireOp",EDGE,"E1.left");var subQ10=sQuery(id+"F0.wireOp",EDGE,"E23.filletArc");var subQ11=sQuery(id+"F0.wireOp",EDGE,"E24.filletArc");Q0=makeQuery(id+"F2.boolean.opBoolean","SPLIT",FACE,{"disambiguationData":[TD([makeQuery(id+"F1.opExtrude","SWEPT_FACE",FACE,{"disambiguationData":[OSD([subQ6])]})])],"derivedFrom":makeQuery(id+"F1.opExtrude","CAP_FACE",FACE,{"disambiguationData":[OSD([subQ6,subQ8,subQ9,subQ7,subQ4,subQ3,subQ2,subQ1,subQ0,subQ5,subQ10,subQ11])],"isStart":true})});}
            var sketch = newSketch(context, id + "F16", { "sketchPlane" : qUnion([Q0])});
            skCircle(sketch, "E79.0", {"center": v(-60, 67.5) * mm, "radius": 4 * mm});
            skArc(sketch, "E79.2", {"start": v(-70, 90) * mm, "mid": v(-77.07, 87.07) * mm, "end": v(-80, 80) * mm});
            skLineSegment(sketch, "E79.3", {"start": v(-80, -80) * mm, "end": v(-80, 80) * mm});
            skArc(sketch, "E79.4", {"start": v(80, 80) * mm, "mid": v(77.07, 87.07) * mm, "end": v(70, 90) * mm});
            skLineSegment(sketch, "E79.5", {"start": v(80, -80) * mm, "end": v(80, 80) * mm});
            skArc(sketch, "E79.6", {"start": v(56.15, 48.18) * mm, "mid": v(0, 67.5) * mm, "end": v(-56.15, 48.18) * mm});
            skArc(sketch, "E79.7", {"start": v(60, 40.3) * mm, "mid": v(58.99, 44.68) * mm, "end": v(56.15, 48.18) * mm});
            skLineSegment(sketch, "E79.8", {"start": v(60, 40.3) * mm, "end": v(60, -40.3) * mm});
            skArc(sketch, "E79.9", {"start": v(-56.15, 48.18) * mm, "mid": v(-58.99, 44.68) * mm, "end": v(-60, 40.3) * mm});
            skLineSegment(sketch, "E79.10", {"start": v(-60, 40.3) * mm, "end": v(-60, -40.3) * mm});
            skLineSegment(sketch, "E79.11", {"start": v(-70, -90) * mm, "end": v(70, -90) * mm});
            skArc(sketch, "E79.12", {"start": v(-80, -80) * mm, "mid": v(-77.07, -87.07) * mm, "end": v(-70, -90) * mm});
            skArc(sketch, "E79.13", {"start": v(70, -90) * mm, "mid": v(77.07, -87.07) * mm, "end": v(80, -80) * mm});
            skArc(sketch, "E79.14", {"start": v(-56.15, -48.18) * mm, "mid": v(0, -67.5) * mm, "end": v(56.15, -48.18) * mm});
            skArc(sketch, "E79.15", {"start": v(56.15, -48.18) * mm, "mid": v(58.99, -44.68) * mm, "end": v(60, -40.3) * mm});
            skArc(sketch, "E79.16", {"start": v(-60, -40.3) * mm, "mid": v(-58.99, -44.68) * mm, "end": v(-56.15, -48.18) * mm});
            skCircle(sketch, "E79.17", {"center": v(-60, -67.5) * mm, "radius": 4 * mm});
            skCircle(sketch, "E79.18", {"center": v(60, -67.5) * mm, "radius": 4 * mm});
            skCircle(sketch, "E79.19", {"center": v(60, 67.5) * mm, "radius": 4 * mm});
            skLineSegment(sketch, "E80", {"start": v(-28.56, 90) * mm, "end": v(-15, 108) * mm});
            skLineSegment(sketch, "E81", {"start": v(-15, 108) * mm, "end": v(-15, 120) * mm});
            skLineSegment(sketch, "E82", {"start": v(33, 90) * mm, "end": v(15, 108) * mm});
            skLineSegment(sketch, "E83", {"start": v(15, 108) * mm, "end": v(15, 120) * mm});
            skArc(sketch, "E84", {"start": v(15, 120) * mm, "mid": v(0, 135) * mm, "end": v(-15, 120) * mm});
            skCircle(sketch, "E85", {"center": v(0, 120) * mm, "radius": 6 * mm});
            skLineSegment(sketch, "E86", {"start": v(0, 120) * mm, "end": v(0, 23.75) * mm, "construction": true});
            skLineSegment(sketch, "E87", {"start": v(-80, 0) * mm, "end": v(80, 0) * mm, "construction": true});
            skLineSegment(sketch, "E88.MirrorCS", {"start": v(-28.56, -90) * mm, "end": v(-15, -108) * mm});
            skLineSegment(sketch, "E89.MirrorCS", {"start": v(-15, -108) * mm, "end": v(-15, -120) * mm});
            skArc(sketch, "E90.MirrorCS", {"start": v(15, -120) * mm, "mid": v(0, -135) * mm, "end": v(-15, -120) * mm});
            skLineSegment(sketch, "E91.MirrorCS", {"start": v(15, -108) * mm, "end": v(15, -120) * mm});
            skLineSegment(sketch, "E92.MirrorCS", {"start": v(33, -90) * mm, "end": v(15, -108) * mm});
            skLineSegment(sketch, "E93.MirrorCS", {"start": v(0, -120) * mm, "end": v(0, -23.75) * mm, "construction": true});
            skCircle(sketch, "E94.MirrorC", {"center": v(0, -120) * mm, "radius": 6 * mm});
            skSolve(sketch);
        }
        {
            var Q0;
            Q0=makeQuery(id+"F16.imprint","IMPRINT",FACE,{"disambiguationData":[TD([[makeQuery(id+"F16.imprint","IMPRINT",EDGE,{"derivedFrom":sQuery(id+"F16.wireOp",EDGE,"E79.0")}),-1.0]])]});
            var Q1;
            {var subQ0=sQuery(id+"F16.wireOp",EDGE,"E88.MirrorCS");Q1=makeQuery(id+"F16.imprint","IMPRINT",FACE,{"disambiguationData":[TD([[makeQuery(id+"F16.imprint","IMPRINT",EDGE,{"derivedFrom":subQ0}),1.0]])]});}
            var Q2;
            {var subQ0=sQuery(id+"F16.wireOp",EDGE,"E80");Q2=makeQuery(id+"F16.imprint","IMPRINT",FACE,{"disambiguationData":[TD([[makeQuery(id+"F16.imprint","IMPRINT",EDGE,{"derivedFrom":subQ0}),-1.0]])]});}
            var Q3;
            Q3=makeQuery(id+"F2.opExtrude","CAP_FACE",FACE,{"disambiguationData":[OSD([sQuery(id+"F0.wireOp",EDGE,"E12"),sQuery(id+"F0.wireOp",EDGE,"E13"),sQuery(id+"F0.wireOp",EDGE,"E14"),sQuery(id+"F0.wireOp",EDGE,"E15"),sQuery(id+"F0.wireOp",EDGE,"E17.filletArc"),sQuery(id+"F0.wireOp",EDGE,"E18.filletArc"),sQuery(id+"F0.wireOp",EDGE,"E19.filletArc"),sQuery(id+"F0.wireOp",EDGE,"E20.filletArc"),sQuery(id+"F0.wireOp",EDGE,"E25.0"),sQuery(id+"F0.wireOp",EDGE,"E25.1"),sQuery(id+"F0.wireOp",EDGE,"E25.2"),sQuery(id+"F0.wireOp",EDGE,"E25.3"),sQuery(id+"F0.wireOp",EDGE,"E25.4"),sQuery(id+"F0.wireOp",EDGE,"E25.5"),sQuery(id+"F0.wireOp",EDGE,"E25.6"),sQuery(id+"F0.wireOp",EDGE,"E25.7")])],"isStart":false});
            extrude(context, id + "F17", {"entities" : qUnion([Q0, Q1, Q2]), "endBound" : BoundingType.UP_TO_SURFACE, "depth" : 25 * mm, "endBoundEntityFace" : qUnion([Q3]), "offsetDistance" : 25 * mm});
        }
    });
